# Revit family: MI-G-AD
name_source: partatom
category: Mechanical Equipment
revit_build: Autodesk Revit 2018 (Build: 20170223_1515(x64)
units: mm (PartAtom-declared; Revit-internal decimal feet)

## family parameters
Always vertical = Yes
Cut with Voids When Loaded = No
OmniClass Number = 23.75.00.00
OmniClass Title = Climate Control (HVAC)
Part Type = Normal
Room Calculation Point = No
Round Connector Dimension = Use Diameter
Shared = No
Work Plane-Based = No

## types (7) — shared parameters
Description = AUTOMATIC RECOVERY GREASE INTERCEPTOR
Manufacturer = MIFAB
URL = WWW.MIFAB.COM

## per-type parameters (varying)
| type | A Length | B Width | Box1 Height | Box1 Width | C1 | C2 | E Height | Grease Container Height | Grease Container Width | Inlet Dia |
| MI-G-AD-15 | 2' - 0 1/2" | 1' - 2" | 0' - 10" | 0' - 4 1/4" | 0' - 4" | 0' - 9" | 1' - 1 1/2" | 0' - 8" | 0' - 8" | 0' - 2" |
| MI-G-AD-20 | 2' - 0 1/2" | 1' - 2" | 0' - 10" | 0' - 4 1/4" | 0' - 4" | 0' - 7 1/2" | 1' - 1 1/2" | 0' - 8" | 0' - 8" | 0' - 2" |
| MI-G-AD-25 | 2' - 2" | 2' - 10" | 0' - 10" | 0' - 4 1/4" | 1' - 3 3/4" | 0' - 6 3/4" | 1' - 6" | 0' - 8" | 0' - 8" | 0' - 3" |
| MI-G-AD-35 | 2' - 10 1/2" | 1' - 4" | 1' - 0" | 0' - 6" | 0' - 8" | 0' - 6 1/4" | 1' - 4 1/2" | 0' - 10" | 0' - 10" | 0' - 3" |
| MI-G-AD-50 | 3' - 3 1/2" | 1' - 4" | 1' - 0" | 0' - 7" | 0' - 5" | 0' - 8 1/2" | 1' - 5 1/2" | 0' - 10" | 0' - 10" | 0' - 3" |
| MI-G-AD-75 | 3' - 7 1/2" | 1' - 4" | 1' - 4" | 0' - 8 1/2" | 0' - 5" | 0' - 9" | 1' - 9 1/2" | 1' - 0" | 0' - 10 1/2" | 0' - 4" |
| MI-G-AD-100 | 5' - 0" | 1' - 9" | 1' - 8" | 1' - 0" | 0' - 4 1/2" | 0' - 9" | 2' - 0 1/2" | 1' - 3" | 1' - 3" | 0' - 4" |

note: column(s) folded — value = type name in every type: Model

## geometry (parser evidence)
native form markers: Sweep x14
no freeform markers — native parametric forms only
